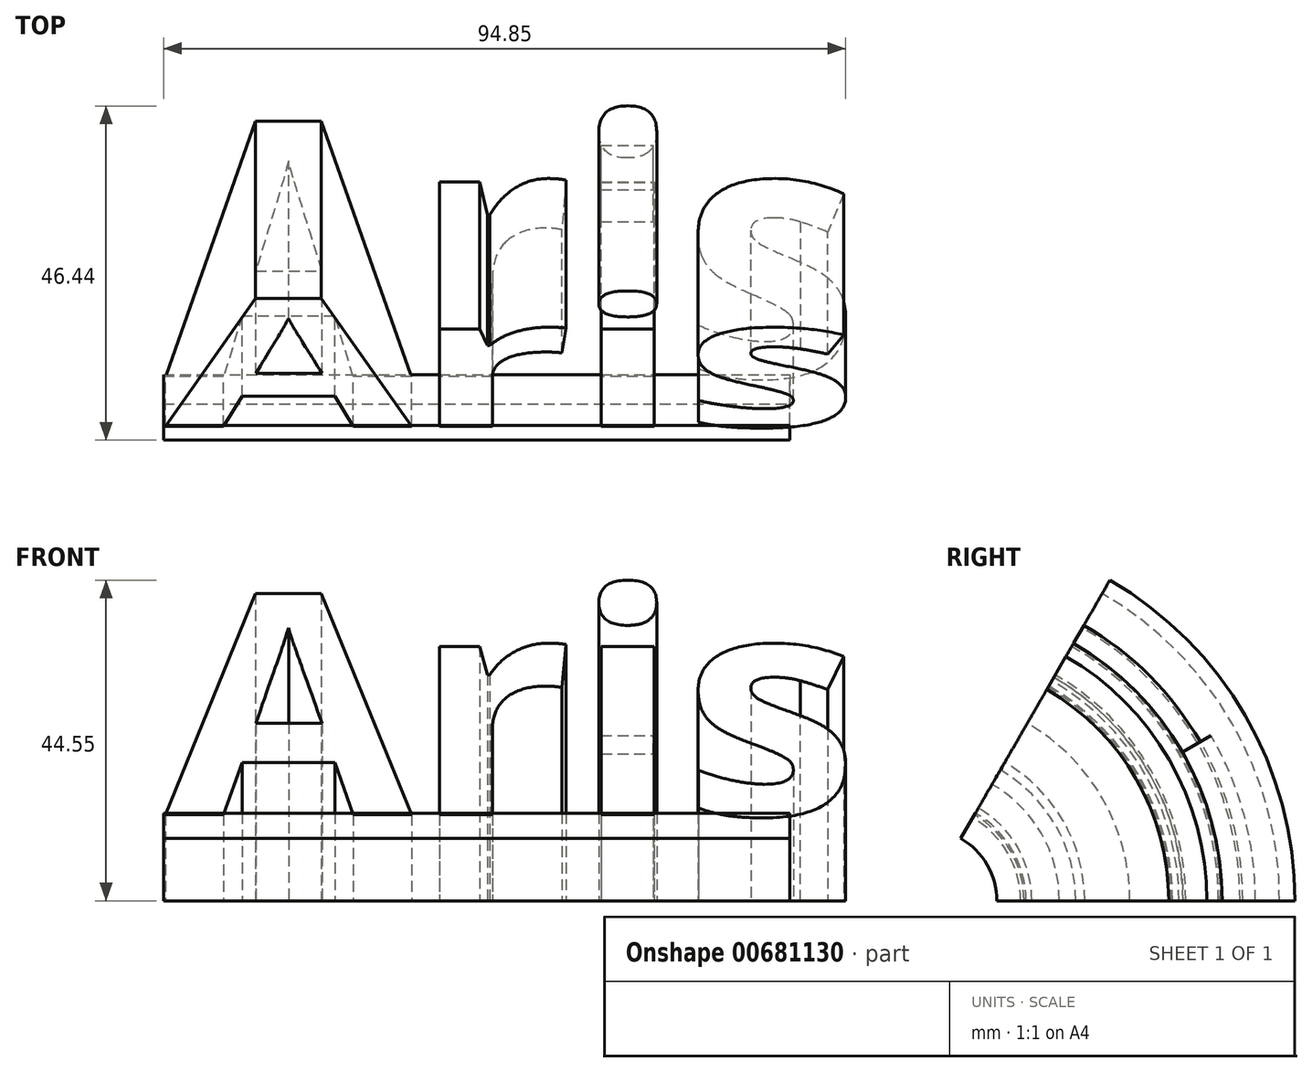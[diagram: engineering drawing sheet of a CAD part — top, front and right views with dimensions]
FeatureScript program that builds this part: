
annotation { "Feature Type Name" : "Feature", "Feature Type Description" : "" }
export const myFeature = defineFeature(function(context is Context, id is Id, definition is map)
    precondition{}
    {
        {
            var Q0;
            Q0=qCreatedBy(makeId("Top.planeOp"),FACE);
            var sketch = newSketch(context, id + "F0", { "sketchPlane" : qUnion([Q0])});
            skText(sketch, "E0", { "text": "Aris", "fontName": "OpenSans-Bold.ttf"});
            const initialGuessF0  = {"E0": [-0.0767, -0.01858, 1, 0, 0.03568]};
            skSetInitialGuess(sketch, initialGuessF0);
            skSolve(sketch);
        }
        {
            var Q0;
            Q0=qCreatedBy(makeId("Top.planeOp"),FACE);
            var sketch = newSketch(context, id + "F1", { "sketchPlane" : qUnion([Q0])});
            skLineSegment(sketch, "E1.bottom", {"start": v(-76.98, -18.31) * mm, "end": v(10.07, -18.31) * mm});
            skLineSegment(sketch, "E1.top", {"start": v(-76.98, -22.37) * mm, "end": v(10.07, -22.37) * mm});
            skLineSegment(sketch, "E1.left", {"start": v(-76.98, -18.31) * mm, "end": v(-76.98, -22.37) * mm});
            skLineSegment(sketch, "E1.right", {"start": v(10.07, -18.31) * mm, "end": v(10.07, -22.37) * mm});
            skSolve(sketch);
        }
        {
            var Q0;
            Q0=qCreatedBy(makeId("Top.planeOp"),FACE);
            var sketch = newSketch(context, id + "F2", { "sketchPlane" : qUnion([Q0])});
            skLineSegment(sketch, "E2.bottom", {"start": v(-16.15, 8.45) * mm, "end": v(-8.86, 8.45) * mm});
            skLineSegment(sketch, "E2.top", {"start": v(-16.15, 13.58) * mm, "end": v(-8.86, 13.58) * mm});
            skLineSegment(sketch, "E2.left", {"start": v(-16.15, 8.45) * mm, "end": v(-16.15, 13.58) * mm});
            skLineSegment(sketch, "E2.right", {"start": v(-8.86, 8.45) * mm, "end": v(-8.86, 13.58) * mm});
            skSolve(sketch);
        }
        {
            var Q0;
            Q0=qCreatedBy(makeId("Top.planeOp"),FACE);
            var sketch = newSketch(context, id + "F3", { "sketchPlane" : qUnion([Q0])});
            skLineSegment(sketch, "E3", {"start": v(-80.48, -32.37) * mm, "end": v(27.64, -32.37) * mm});
            skSolve(sketch);
        }
        {
            var Q0;
            Q0 = qSketchRegion(id + "F0", true);
            var Q1;
            Q1=makeQuery(id+"F1.imprint","IMPRINT",FACE,{"disambiguationData":[TD([[makeQuery(id+"F1.imprint","IMPRINT",EDGE,{"derivedFrom":sQuery(id+"F1.wireOp",EDGE,"E1.bottom")}),-1.0]])]});
            var Q2;
            Q2=sQuery(id+"F3.wireOp",EDGE,"E3");
            revolve(context, id + "F4", {"surfaceOperationType" : NewSurfaceOperationType.NEW, "entities" : qUnion([Q0, Q1]), "axis" : qUnion([Q2]), "revolveType" : RevolveType.ONE_DIRECTION, "angle" : 60 * degree});
        }
        {
            var Q0;
            Q0=makeQuery(id+"F2.imprint","IMPRINT",FACE,{"disambiguationData":[TD([[makeQuery(id+"F2.imprint","IMPRINT",EDGE,{"derivedFrom":sQuery(id+"F2.wireOp",EDGE,"E2.bottom")}),1.0]])]});
            var Q1;
            Q1=sQuery(id+"F3.wireOp",EDGE,"E3");
            revolve(context, id + "F5", {"entities" : qUnion([Q0]), "axis" : qUnion([Q1]), "revolveType" : RevolveType.ONE_DIRECTION, "angle" : 30 * degree});
        }
    });
